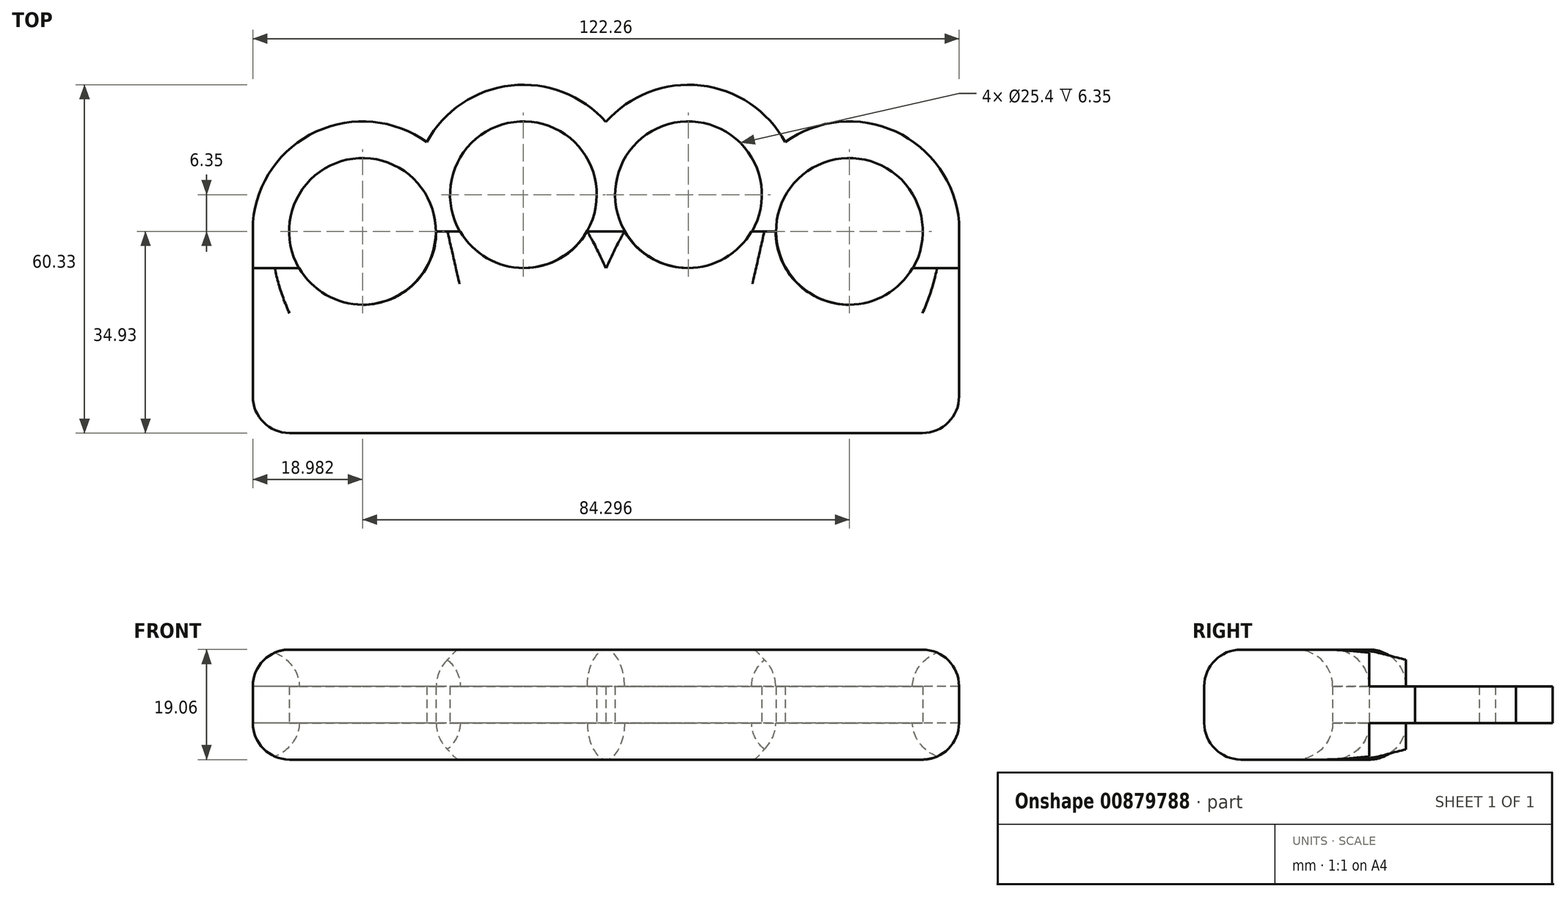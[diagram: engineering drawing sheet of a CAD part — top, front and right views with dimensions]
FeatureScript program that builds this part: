
annotation { "Feature Type Name" : "Feature", "Feature Type Description" : "" }
export const myFeature = defineFeature(function(context is Context, id is Id, definition is map)
    precondition{}
    {
        {
            var Q0;
            Q0=qCreatedBy(makeId("Top.planeOp"),FACE);
            var sketch = newSketch(context, id + "F0", { "sketchPlane" : qUnion([Q0])});
            skLineSegment(sketch, "E0.bottom", {"start": v(61.13, 0) * mm, "end": v(-61.13, 0) * mm});
            skLineSegment(sketch, "E0.top", {"start": v(61.13, 50.8) * mm, "end": v(-61.13, 50.8) * mm, "construction": true});
            skLineSegment(sketch, "E0.left", {"start": v(61.13, 0) * mm, "end": v(61.13, 50.8) * mm});
            skLineSegment(sketch, "E0.right", {"start": v(-61.13, 0) * mm, "end": v(-61.13, 50.8) * mm});
            skPoint(sketch, "E0.middle", {"position": v(0, 25.4) * mm});
            skCircle(sketch, "E1", {"center": v(-14.29, 31.75) * mm, "radius": 12.7 * mm});
            skPoint(sketch, "E2.orphan", {"position": v(-61.13, 25.4) * mm});
            skPoint(sketch, "E3.end.orphan", {"position": v(61.13, 25.4) * mm});
            skCircle(sketch, "E4", {"center": v(-42.15, 25.4) * mm, "radius": 12.7 * mm});
            skCircle(sketch, "E5", {"center": v(14.29, 31.75) * mm, "radius": 12.7 * mm});
            skCircle(sketch, "E6", {"center": v(42.15, 25.4) * mm, "radius": 12.7 * mm});
            skArc(sketch, "E7", {"start": v(-31.02, 40.86) * mm, "mid": v(-16.42, 50.68) * mm, "end": v(0, 44.35) * mm});
            skArc(sketch, "E8", {"start": v(0, 44.35) * mm, "mid": v(16.42, 50.68) * mm, "end": v(31.02, 40.86) * mm});
            skPoint(sketch, "E9.end.orphan", {"position": v(31.02, 40.86) * mm});
            skArc(sketch, "E10", {"start": v(-31.02, 40.86) * mm, "mid": v(-50.83, 42.35) * mm, "end": v(-61.2, 25.4) * mm});
            skArc(sketch, "E11", {"start": v(31.02, 40.86) * mm, "mid": v(50.83, 42.35) * mm, "end": v(61.2, 25.4) * mm});
            skSolve(sketch);
        }
        {
            var Q0;
            {var subQ6=sQuery(id+"F0.wireOp",EDGE,"E0.bottom");Q0=makeQuery(id+"F0.imprint","IMPRINT",FACE,{"disambiguationData":[TD([[makeQuery(id+"F0.imprint","IMPRINT",EDGE,{"derivedFrom":subQ6}),-1.0]])]});}
            extrude(context, id + "F1", {"entities" : qUnion([Q0]), "depth" : 3.17 * mm, "offsetDistance" : 25.4 * mm, "hasSecondDirection" : true, "secondDirectionOppositeDirection" : true, "secondDirectionDepth" : 3.17 * mm});
        }
        {
            var Q0;
            Q0=qCreatedBy(makeId("Top.planeOp"),FACE);
            var sketch = newSketch(context, id + "F2", { "sketchPlane" : qUnion([Q0])});
            skLineSegment(sketch, "E12.bottom", {"start": v(61.13, -9.53) * mm, "end": v(-61.13, -9.53) * mm});
            skLineSegment(sketch, "E12.top", {"start": v(61.13, 19.05) * mm, "end": v(53.08, 19.05) * mm});
            skLineSegment(sketch, "E12.left", {"start": v(61.13, -9.53) * mm, "end": v(61.13, 19.05) * mm});
            skLineSegment(sketch, "E12.right", {"start": v(-61.13, -9.53) * mm, "end": v(-61.13, 19.05) * mm});
            skPoint(sketch, "E12.middle", {"position": v(0, 4.76) * mm});
            skArc(sketch, "E13", {"start": v(53.08, 19.05) * mm, "mid": v(38.8, 13.13) * mm, "end": v(29.38, 25.4) * mm});
            skLineSegment(sketch, "E14.trimOffspring", {"start": v(-53.08, 19.05) * mm, "end": v(-61.13, 19.05) * mm});
            skLineSegment(sketch, "E15", {"start": v(61.13, 0) * mm, "end": v(-61.13, 0) * mm});
            skPoint(sketch, "E16.center.orphan", {"position": v(-42.08, 25.4) * mm});
            skArc(sketch, "E17", {"start": v(-53.08, 19.05) * mm, "mid": v(-38.8, 13.13) * mm, "end": v(-29.38, 25.4) * mm});
            skLineSegment(sketch, "E18", {"start": v(-29.38, 25.4) * mm, "end": v(-25.22, 25.4) * mm});
            skArc(sketch, "E19", {"start": v(-25.22, 25.4) * mm, "mid": v(-14.22, 19.05) * mm, "end": v(-3.22, 25.4) * mm});
            skArc(sketch, "E20", {"start": v(25.22, 25.4) * mm, "mid": v(14.22, 19.05) * mm, "end": v(3.22, 25.4) * mm});
            skLineSegment(sketch, "E21.trimOffspring", {"start": v(25.22, 25.4) * mm, "end": v(29.38, 25.4) * mm});
            skLineSegment(sketch, "E22.trimOffspring", {"start": v(-3.22, 25.4) * mm, "end": v(3.22, 25.4) * mm});
            skSolve(sketch);
        }
        {
            var Q0;
            Q0 = qSketchRegion(id + "F2", true);
            extrude(context, id + "F3", {"entities" : qUnion([Q0]), "depth" : 9.52 * mm, "offsetDistance" : 25.4 * mm, "hasSecondDirection" : true, "secondDirectionOppositeDirection" : false, "secondDirectionDepth" : 3.17 * mm});
        }
        {
            var Q0;
            {var subQ0=sQuery(id+"F2.wireOp",EDGE,"E12.bottom");Q0=makeQuery(id+"F2.imprint","IMPRINT",FACE,{"disambiguationData":[TD([[makeQuery(id+"F2.imprint","IMPRINT",EDGE,{"derivedFrom":subQ0}),-1.0]])]});}
            extrude(context, id + "F4", {"entities" : qUnion([Q0]), "operationType" : NewBodyOperationType.ADD, "depth" : 3.17 * mm, "offsetDistance" : 25.4 * mm, "hasSecondDirection" : true, "secondDirectionOppositeDirection" : true, "secondDirectionDepth" : 3.17 * mm});
        }
        {
            var Q0;
            Q0 = qSketchRegion(id + "F2", true);
            extrude(context, id + "F5", {"entities" : qUnion([Q0]), "operationType" : NewBodyOperationType.ADD, "oppositeDirection" : true, "depth" : 9.52 * mm, "offsetDistance" : 25.4 * mm, "hasSecondDirection" : true, "secondDirectionOppositeDirection" : true, "secondDirectionDepth" : 3.17 * mm});
        }
        {
            var Q0;
            Q0=makeQuery(id+"F3.opExtrude","CAP_FACE",FACE,{"disambiguationData":[OSD([sQuery(id+"F2.wireOp",EDGE,"E12.bottom"),sQuery(id+"F2.wireOp",EDGE,"E12.top"),sQuery(id+"F2.wireOp",EDGE,"E12.left"),sQuery(id+"F2.wireOp",EDGE,"E12.right"),sQuery(id+"F2.wireOp",EDGE,"E13"),sQuery(id+"F2.wireOp",EDGE,"E14.trimOffspring"),sQuery(id+"F2.wireOp",EDGE,"E17"),sQuery(id+"F2.wireOp",EDGE,"E18"),sQuery(id+"F2.wireOp",EDGE,"E19"),sQuery(id+"F2.wireOp",EDGE,"E20"),sQuery(id+"F2.wireOp",EDGE,"E21.trimOffspring"),sQuery(id+"F2.wireOp",EDGE,"E22.trimOffspring")])],"isStart":false});
            var Q1;
            Q1=makeQuery(id+"F5.opExtrude","CAP_FACE",FACE,{"disambiguationData":[OSD([sQuery(id+"F2.wireOp",EDGE,"E12.bottom"),sQuery(id+"F2.wireOp",EDGE,"E12.top"),sQuery(id+"F2.wireOp",EDGE,"E12.left"),sQuery(id+"F2.wireOp",EDGE,"E12.right"),sQuery(id+"F2.wireOp",EDGE,"E13"),sQuery(id+"F2.wireOp",EDGE,"E14.trimOffspring"),sQuery(id+"F2.wireOp",EDGE,"E17"),sQuery(id+"F2.wireOp",EDGE,"E18"),sQuery(id+"F2.wireOp",EDGE,"E19"),sQuery(id+"F2.wireOp",EDGE,"E20"),sQuery(id+"F2.wireOp",EDGE,"E21.trimOffspring"),sQuery(id+"F2.wireOp",EDGE,"E22.trimOffspring")])],"isStart":false});
            fillet(context, id + "F6", {"entities" : qUnion([Q0, Q1]), "radius" : 6.35 * mm, "allowEdgeOverflow" : false});
        }
        {
            var Q0;
            {var subQ0=sQuery(id+"F2.wireOp",EDGE,"E12.left");var subQ1=sQuery(id+"F2.wireOp",EDGE,"E12.bottom");Q0=makeQuery(id+"F5.boolean.opBoolean","MERGE",EDGE,{"derivedFrom":[makeQuery(id+"F4.boolean.opBoolean","MERGE",EDGE,{"derivedFrom":[makeQuery(id+"F3.opExtrude","SWEPT_EDGE",EDGE,{"disambiguationData":[OSD([subQ1,subQ0])]}),makeQuery(id+"F4.opExtrude","SWEPT_EDGE",EDGE,{"disambiguationData":[OSD([subQ1,subQ0])]})]}),makeQuery(id+"F5.opExtrude","SWEPT_EDGE",EDGE,{"disambiguationData":[OSD([subQ1,subQ0])]})]});}
            var Q1;
            {var subQ0=sQuery(id+"F2.wireOp",EDGE,"E12.right");var subQ1=sQuery(id+"F2.wireOp",EDGE,"E12.bottom");Q1=makeQuery(id+"F5.boolean.opBoolean","MERGE",EDGE,{"derivedFrom":[makeQuery(id+"F4.boolean.opBoolean","MERGE",EDGE,{"derivedFrom":[makeQuery(id+"F3.opExtrude","SWEPT_EDGE",EDGE,{"disambiguationData":[OSD([subQ1,subQ0])]}),makeQuery(id+"F4.opExtrude","SWEPT_EDGE",EDGE,{"disambiguationData":[OSD([subQ1,subQ0])]})]}),makeQuery(id+"F5.opExtrude","SWEPT_EDGE",EDGE,{"disambiguationData":[OSD([subQ1,subQ0])]})]});}
            fillet(context, id + "F7", {"entities" : qUnion([Q0, Q1]), "radius" : 6.35 * mm, "tangentPropagation" : true, "allowEdgeOverflow" : false});
        }
    });
